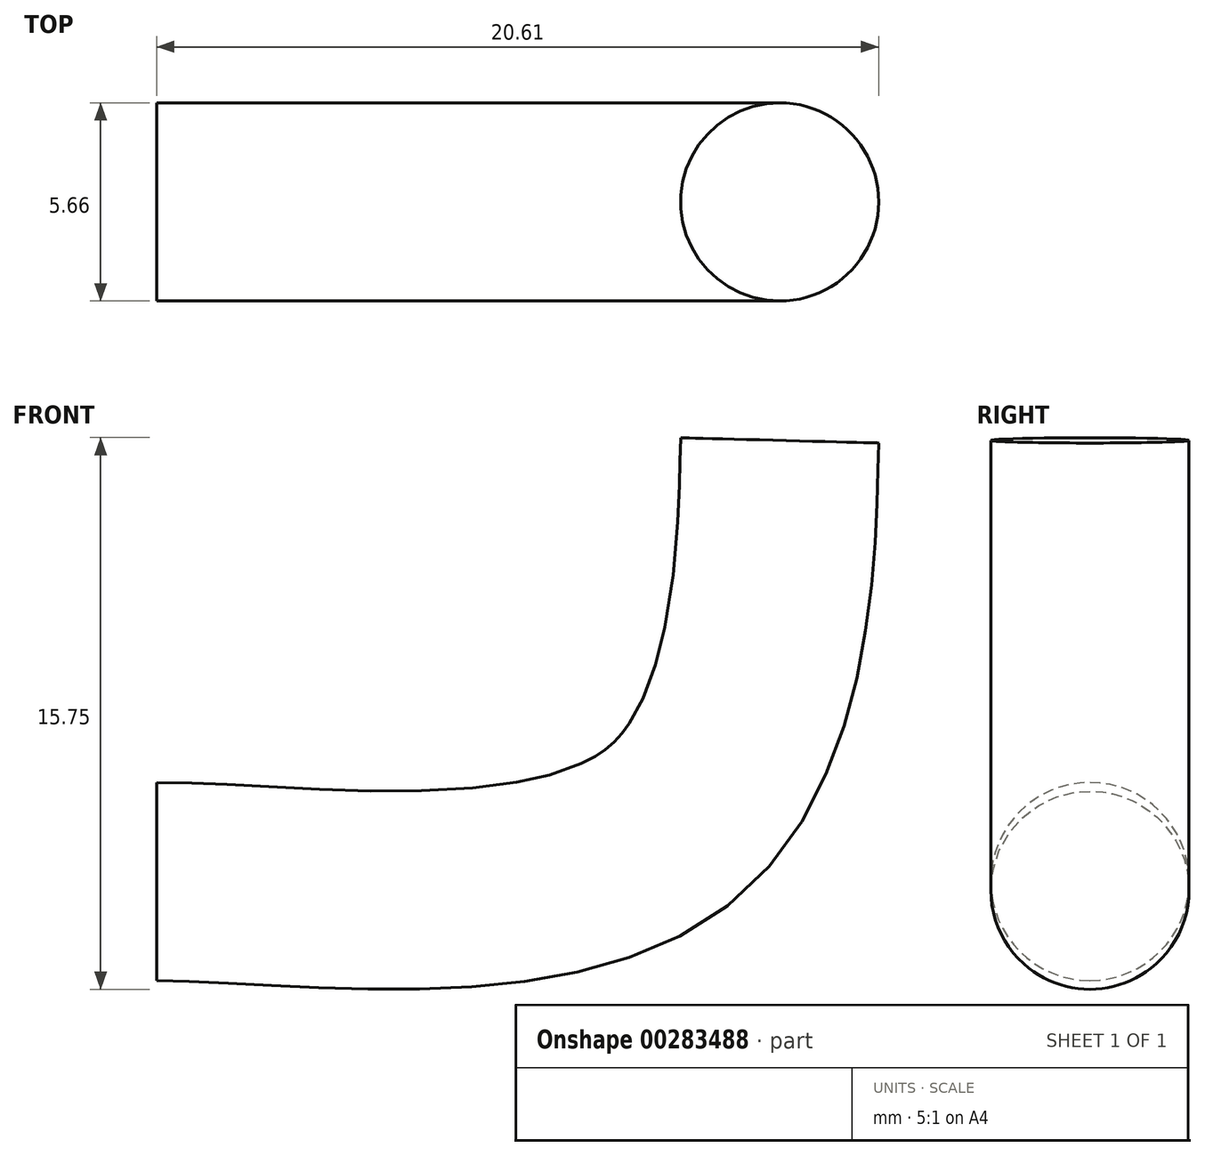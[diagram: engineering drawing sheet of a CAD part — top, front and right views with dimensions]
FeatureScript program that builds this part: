
annotation { "Feature Type Name" : "Feature", "Feature Type Description" : "" }
export const myFeature = defineFeature(function(context is Context, id is Id, definition is map)
    precondition{}
    {
        {
            var Q0;
            Q0=qCreatedBy(makeId("Front.planeOp"),FACE);
            var sketch = newSketch(context, id + "F0", { "sketchPlane" : qUnion([Q0])});
            skFitSpline(sketch, "E0", {"points": [v(0, 0) * mm, v(14.95, 1.8) * mm, v(18, 12.8) * mm], "startDerivative": vector(22.15, 0) * mm, "endDerivative": vector(0.42, 15.98) * mm});
            skSolve(sketch);
        }
        {
            var Q0;
            Q0=qCreatedBy(makeId("Right.planeOp"),FACE);
            var sketch = newSketch(context, id + "F1", { "sketchPlane" : qUnion([Q0])});
            skCircle(sketch, "E1", {"center": v(0, 0.22) * mm, "radius": 2.83 * mm});
            skSolve(sketch);
        }
        {
            var Q0;
            Q0=makeQuery(id+"F1.imprint","IMPRINT",FACE,{"disambiguationData":[TD([[makeQuery(id+"F1.imprint","IMPRINT",EDGE,{"derivedFrom":sQuery(id+"F1.wireOp",EDGE,"E1")}),1.0]])]});
            var Q1;
            Q1=sQuery(id+"F0.wireOp",EDGE,"E0");
            sweep(context, id + "F2", {"profiles" : qUnion([Q0]), "path" : qUnion([Q1])});
        }
    });
